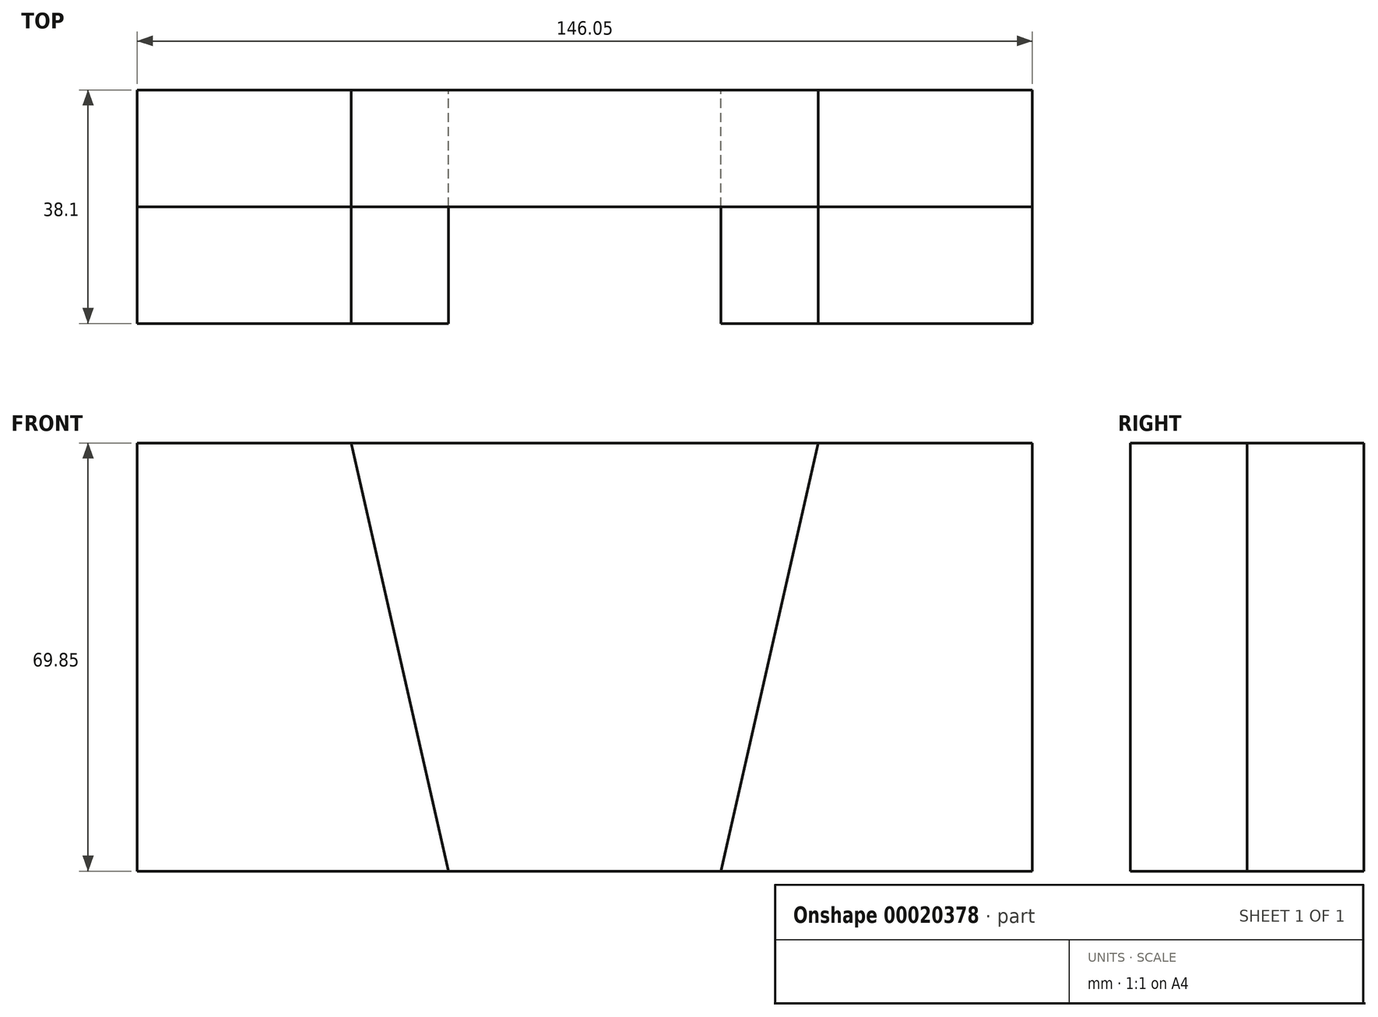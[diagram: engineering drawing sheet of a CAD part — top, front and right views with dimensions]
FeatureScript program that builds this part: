
annotation { "Feature Type Name" : "Feature", "Feature Type Description" : "" }
export const myFeature = defineFeature(function(context is Context, id is Id, definition is map)
    precondition{}
    {
        {
            var Q0;
            Q0=qCreatedBy(makeId("Front.planeOp"),FACE);
            var sketch = newSketch(context, id + "F0", { "sketchPlane" : qUnion([Q0])});
            skLineSegment(sketch, "E0", {"start": v(-77.9, 40.06) * mm, "end": v(-77.9, -29.79) * mm});
            skLineSegment(sketch, "E1", {"start": v(-77.9, -29.79) * mm, "end": v(-27.1, -29.79) * mm});
            skLineSegment(sketch, "E2", {"start": v(-77.9, 40.06) * mm, "end": v(-42.97, 40.06) * mm});
            skLineSegment(sketch, "E3", {"start": v(-42.97, 40.06) * mm, "end": v(-27.1, -29.79) * mm});
            skLineSegment(sketch, "E4", {"start": v(17.35, -29.79) * mm, "end": v(68.15, -29.79) * mm});
            skLineSegment(sketch, "E5", {"start": v(68.15, -29.79) * mm, "end": v(68.15, 40.06) * mm});
            skLineSegment(sketch, "E6", {"start": v(68.15, 40.06) * mm, "end": v(33.23, 40.06) * mm});
            skLineSegment(sketch, "E7", {"start": v(17.35, -29.79) * mm, "end": v(33.23, 40.06) * mm});
            skLineSegment(sketch, "E8", {"start": v(-42.97, 40.06) * mm, "end": v(33.23, 40.06) * mm});
            skLineSegment(sketch, "E9", {"start": v(-27.1, -29.79) * mm, "end": v(17.35, -29.79) * mm});
            skSolve(sketch);
        }
        {
            var Q0;
            Q0=makeQuery(id+"F0.imprint","IMPRINT",FACE,{"disambiguationData":[TD([[makeQuery(id+"F0.imprint","IMPRINT",EDGE,{"derivedFrom":sQuery(id+"F0.wireOp",EDGE,"E0")}),1.0]])]});
            extrude(context, id + "F1", {"entities" : qUnion([Q0]), "depth" : 38.1 * mm});
        }
        {
            var Q0;
            Q0=makeQuery(id+"F0.imprint","IMPRINT",FACE,{"disambiguationData":[TD([[makeQuery(id+"F0.imprint","IMPRINT",EDGE,{"derivedFrom":sQuery(id+"F0.wireOp",EDGE,"E4")}),1.0]])]});
            extrude(context, id + "F2", {"entities" : qUnion([Q0]), "depth" : 38.1 * mm});
        }
        {
            var Q0;
            Q0=makeQuery(id+"F0.imprint","IMPRINT",FACE,{"disambiguationData":[TD([[makeQuery(id+"F0.imprint","IMPRINT",EDGE,{"derivedFrom":sQuery(id+"F0.wireOp",EDGE,"E0")}),1.0]])]});
            var Q1;
            Q1=makeQuery(id+"F0.imprint","IMPRINT",FACE,{"disambiguationData":[TD([[makeQuery(id+"F0.imprint","IMPRINT",EDGE,{"derivedFrom":sQuery(id+"F0.wireOp",EDGE,"E4")}),1.0]])]});
            var Q2;
            Q2=makeQuery(id+"F0.imprint","IMPRINT",FACE,{"disambiguationData":[TD([[makeQuery(id+"F0.imprint","IMPRINT",EDGE,{"derivedFrom":sQuery(id+"F0.wireOp",EDGE,"E3")}),1.0]])]});
            extrude(context, id + "F3", {"entities" : qUnion([Q0, Q1, Q2]), "depth" : 19.05 * mm});
        }
    });
